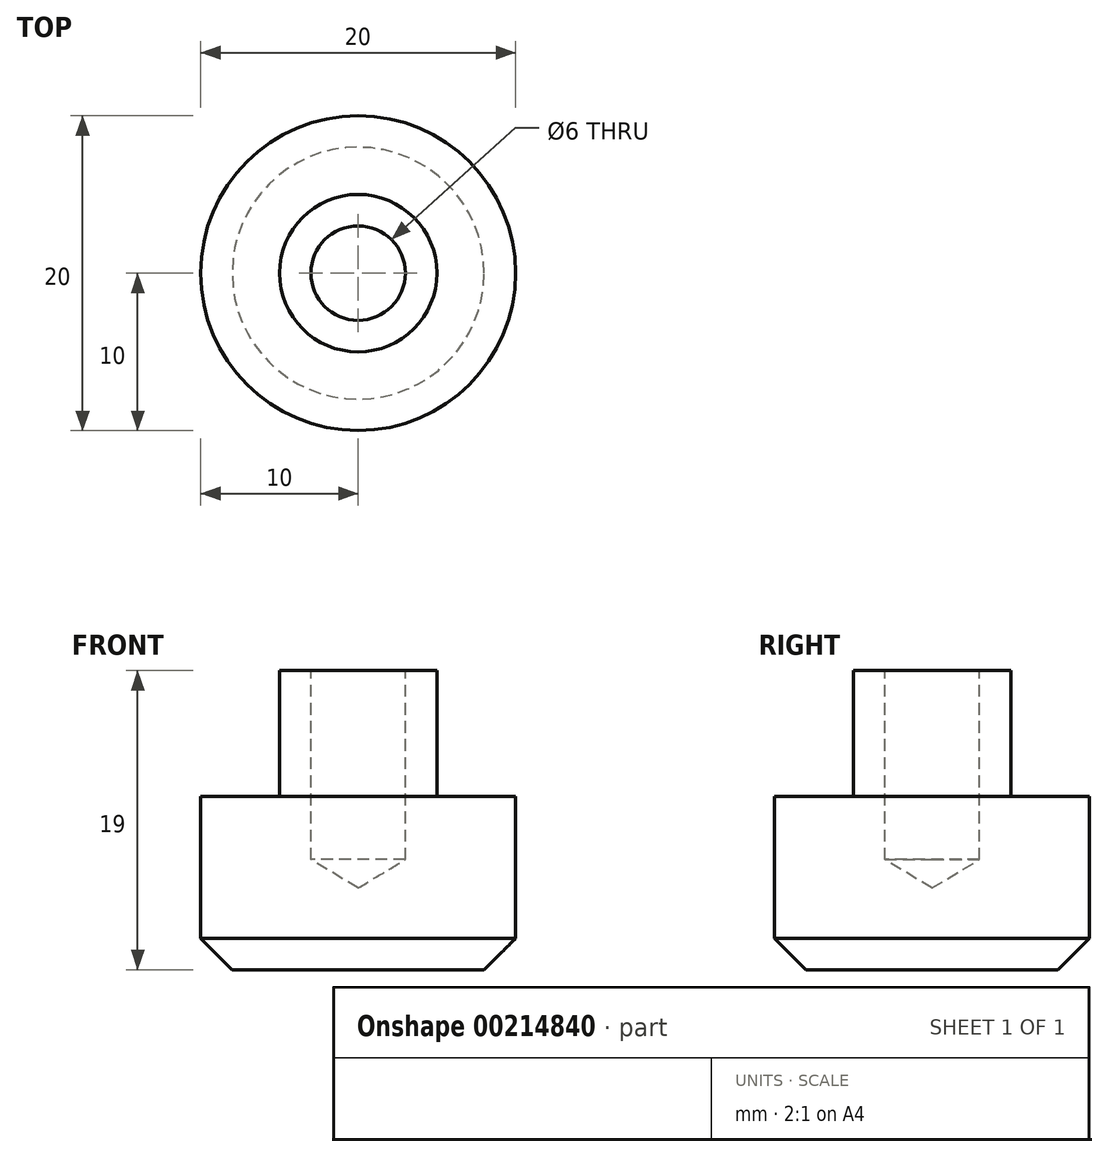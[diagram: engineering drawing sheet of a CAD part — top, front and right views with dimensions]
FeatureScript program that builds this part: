
annotation { "Feature Type Name" : "Feature", "Feature Type Description" : "" }
export const myFeature = defineFeature(function(context is Context, id is Id, definition is map)
    precondition{}
    {
        {
            var Q0;
            Q0=qCreatedBy(makeId("Top.planeOp"),FACE);
            var sketch = newSketch(context, id + "F0", { "sketchPlane" : qUnion([Q0])});
            skCircle(sketch, "E0", {"center": v(0, 0) * mm, "radius": 10 * mm});
            skSolve(sketch);
        }
        {
            var Q0;
            Q0=makeQuery(id+"F0.imprint","IMPRINT",FACE,{"disambiguationData":[TD([[makeQuery(id+"F0.imprint","IMPRINT",EDGE,{"derivedFrom":sQuery(id+"F0.wireOp",EDGE,"E0")}),1.0]])]});
            extrude(context, id + "F1", {"entities" : qUnion([Q0]), "depth" : 11 * mm});
        }
        {
            var Q0;
            Q0=makeQuery(id+"F1.opExtrude","CAP_FACE",FACE,{"disambiguationData":[OSD([sQuery(id+"F0.wireOp",EDGE,"E0")])],"isStart":false});
            var sketch = newSketch(context, id + "F2", { "sketchPlane" : qUnion([Q0])});
            skCircle(sketch, "E1", {"center": v(0, 0) * mm, "radius": 5 * mm});
            skSolve(sketch);
        }
        {
            var Q0;
            Q0=makeQuery(id+"F2.imprint","IMPRINT",FACE,{"disambiguationData":[TD([[makeQuery(id+"F2.imprint","IMPRINT",EDGE,{"derivedFrom":sQuery(id+"F2.wireOp",EDGE,"E1")}),1.0]])]});
            extrude(context, id + "F3", {"entities" : qUnion([Q0]), "operationType" : NewBodyOperationType.ADD, "depth" : 8 * mm});
        }
        {
            var Q0;
            Q0=makeQuery(id+"F3.opExtrude","CAP_FACE",FACE,{"disambiguationData":[OSD([sQuery(id+"F2.wireOp",EDGE,"E1")])],"isStart":false});
            var sketch = newSketch(context, id + "F4", { "sketchPlane" : qUnion([Q0])});
            skPoint(sketch, "E2", {"position": v(0, 0) * mm});
            skSolve(sketch);
        }
        {
            var Q0;
            Q0=sQuery(id+"F4.wireOp",VERTEX,"E2");
            var Q1;
            Q1=makeQuery(id+"F1.opExtrude","SWEPT_BODY",BODY,{"disambiguationData":[OSD([sQuery(id+"F0.wireOp",EDGE,"E0")])]});
            hole(context, id + "F5", {"style" : HoleStyle.SIMPLE, "endStyle" : HoleEndStyle.BLIND, "holeDiameter" : 6 * mm, "holeDepth" : 12 * mm, "startFromSketch" : true, "locations" : qUnion([Q0]), "scope" : qUnion([Q1])});
        }
        {
            var Q0;
            Q0=makeQuery(id+"F1.opExtrude","CAP_EDGE",EDGE,{"disambiguationData":[OSD([sQuery(id+"F0.wireOp",EDGE,"E0")])],"isStart":true});
            chamfer(context, id + "F6", {"entities" : qUnion([Q0]), "width" : 2 * mm, "tangentPropagation" : true});
        }
    });
